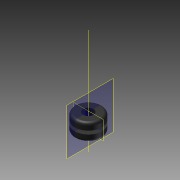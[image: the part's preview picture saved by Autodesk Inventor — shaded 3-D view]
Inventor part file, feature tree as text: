
AUTODESK INVENTOR PART (.ipt)
format: ipt  version: 2014 (Build 180170000, 170)  size: 132,608 bytes
history: native  units: in
note: dims shown in document units (in); Inventor stores cm internally (conversion verified against a paired STEP export)
features: plane x2, revolve x1, sketch x1, other x1
ambient origin geometry x8: Origin, YZ Plane, XZ Plane, XY Plane, X Axis, Y Axis, Z Axis, Center Point
bodies: Solid1 (feature_tree)
feature tree (5):
  plane  "Work Plane2"
  revolve  "Revolution1"  Angle=90.0deg
  plane  "Work Plane3"
  sketch  "Sketch2"  dims[d0=0.05in d1=90.0deg d2=0.05in d4=0.1562in d5=0.3125in d6=90.0deg]
  other  "Work Axis2"
